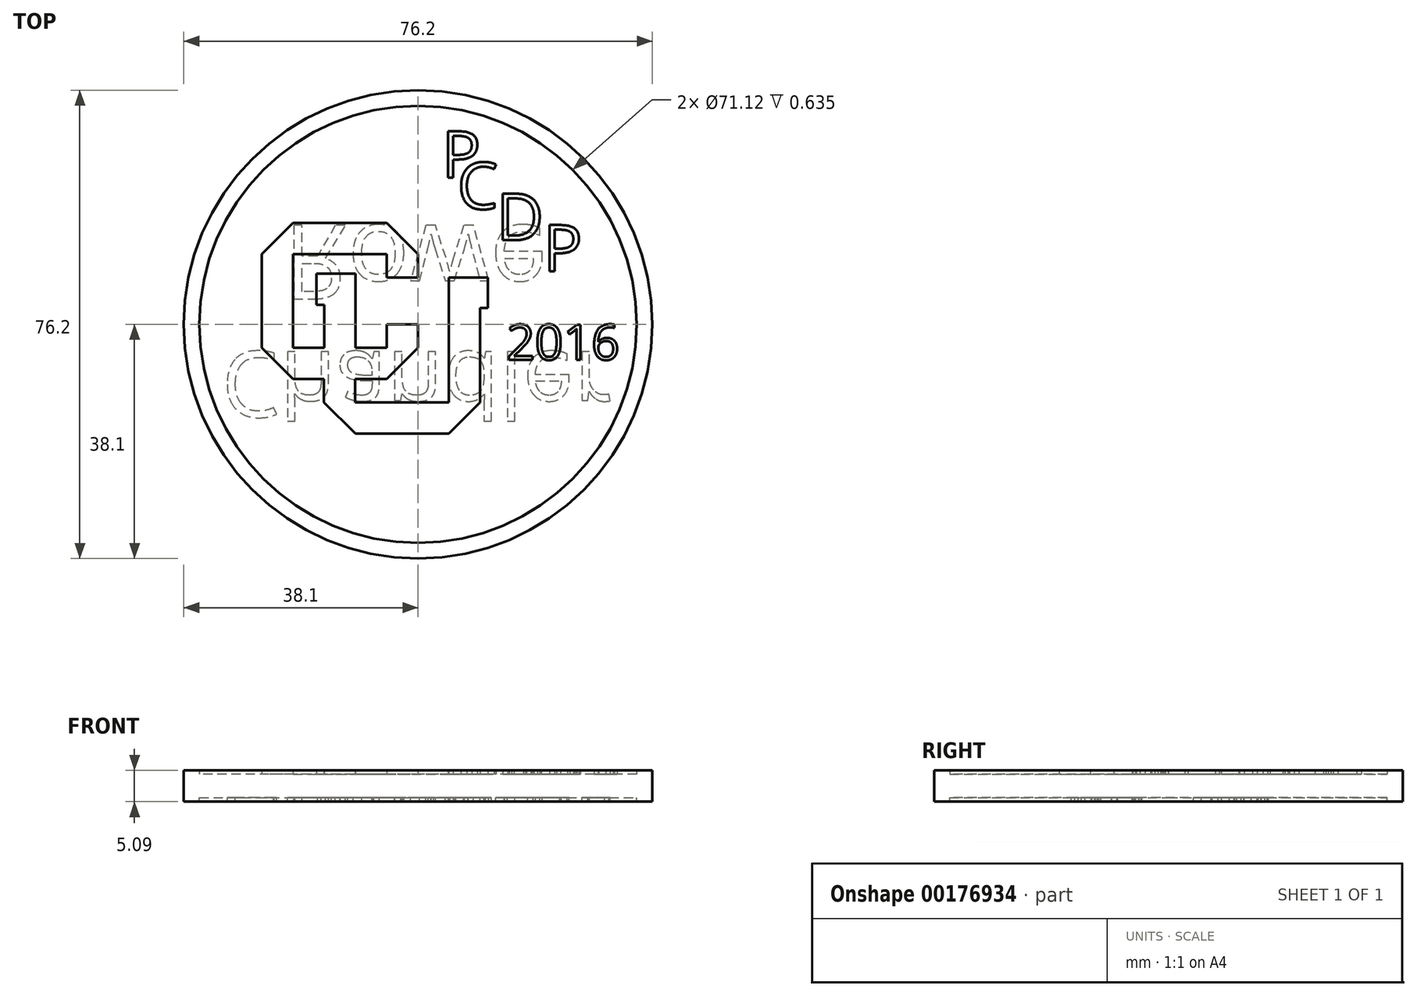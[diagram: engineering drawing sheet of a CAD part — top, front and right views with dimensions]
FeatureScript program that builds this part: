
annotation { "Feature Type Name" : "Feature", "Feature Type Description" : "" }
export const myFeature = defineFeature(function(context is Context, id is Id, definition is map)
    precondition{}
    {
        {
            var Q0;
            Q0=qCreatedBy(makeId("Top.planeOp"),FACE);
            var sketch = newSketch(context, id + "F0", { "sketchPlane" : qUnion([Q0])});
            skCircle(sketch, "E0", {"center": v(0, 0) * mm, "radius": 38.1 * mm});
            skSolve(sketch);
        }
        {
            var Q0;
            Q0=makeQuery(id+"F0.imprint","IMPRINT",FACE,{"disambiguationData":[TD([[makeQuery(id+"F0.imprint","IMPRINT",EDGE,{"derivedFrom":sQuery(id+"F0.wireOp",EDGE,"E0")}),1.0]])]});
            extrude(context, id + "F1", {"entities" : qUnion([Q0]), "depth" : 3.8 * mm});
        }
        {
            var Q0;
            Q0=makeQuery(id+"F1.opExtrude","CAP_FACE",FACE,{"disambiguationData":[OSD([sQuery(id+"F0.wireOp",EDGE,"E0")])],"isStart":false});
            var sketch = newSketch(context, id + "F2", { "sketchPlane" : qUnion([Q0])});
            skLineSegment(sketch, "E1", {"start": v(0, 0) * mm, "end": v(0, -3.81) * mm});
            skLineSegment(sketch, "E2", {"start": v(-5.08, -8.9) * mm, "end": v(0, -3.81) * mm});
            skLineSegment(sketch, "E3", {"start": v(-5.08, -8.9) * mm, "end": v(-20.32, -8.9) * mm});
            skLineSegment(sketch, "E4", {"start": v(-20.32, -8.9) * mm, "end": v(-25.4, -3.81) * mm});
            skLineSegment(sketch, "E5", {"start": v(-25.4, 11.43) * mm, "end": v(-20.32, 16.5) * mm});
            skLineSegment(sketch, "E6", {"start": v(-20.32, 16.5) * mm, "end": v(-5.08, 16.5) * mm});
            skLineSegment(sketch, "E7", {"start": v(-5.08, 16.5) * mm, "end": v(0, 11.43) * mm});
            skLineSegment(sketch, "E8", {"start": v(0, 11.43) * mm, "end": v(0, 7.62) * mm});
            skLineSegment(sketch, "E9", {"start": v(-25.4, 11.43) * mm, "end": v(-25.4, -3.81) * mm});
            skLineSegment(sketch, "E10", {"start": v(0, 7.62) * mm, "end": v(-5.08, 7.62) * mm});
            skLineSegment(sketch, "E11", {"start": v(-5.08, 7.62) * mm, "end": v(-5.08, 11.43) * mm});
            skLineSegment(sketch, "E12", {"start": v(-5.08, 11.43) * mm, "end": v(-20.32, 11.43) * mm});
            skLineSegment(sketch, "E13", {"start": v(-20.32, 11.43) * mm, "end": v(-20.32, -3.81) * mm});
            skLineSegment(sketch, "E14", {"start": v(-5.08, -3.81) * mm, "end": v(-5.08, 0) * mm});
            skLineSegment(sketch, "E15", {"start": v(-5.08, 0) * mm, "end": v(0, 0) * mm});
            skLineSegment(sketch, "E16", {"start": v(-5.08, -3.81) * mm, "end": v(-10.16, -3.81) * mm});
            skLineSegment(sketch, "E17", {"start": v(-10.16, -3.81) * mm, "end": v(-10.16, 8.25) * mm});
            skLineSegment(sketch, "E18", {"start": v(-10.16, 8.25) * mm, "end": v(-16.51, 8.25) * mm});
            skLineSegment(sketch, "E19", {"start": v(-16.51, 8.25) * mm, "end": v(-16.51, 3.17) * mm});
            skLineSegment(sketch, "E20", {"start": v(-16.51, 3.17) * mm, "end": v(-15.24, 3.17) * mm});
            skLineSegment(sketch, "E21", {"start": v(-15.24, 3.17) * mm, "end": v(-15.24, -3.81) * mm});
            skLineSegment(sketch, "E22.trimOffspring", {"start": v(-15.24, -3.81) * mm, "end": v(-20.32, -3.81) * mm});
            skLineSegment(sketch, "E23", {"start": v(-15.3, -8.9) * mm, "end": v(-15.3, -12.69) * mm});
            skLineSegment(sketch, "E24", {"start": v(-15.3, -12.69) * mm, "end": v(-10.19, -17.77) * mm});
            skLineSegment(sketch, "E25", {"start": v(-10.19, -17.77) * mm, "end": v(5.03, -17.77) * mm});
            skLineSegment(sketch, "E26", {"start": v(5.03, -17.77) * mm, "end": v(10.1, -12.69) * mm});
            skLineSegment(sketch, "E27", {"start": v(10.1, -12.69) * mm, "end": v(10.1, 2.68) * mm});
            skLineSegment(sketch, "E28", {"start": v(10.1, 2.68) * mm, "end": v(11.38, 2.68) * mm});
            skLineSegment(sketch, "E29", {"start": v(11.38, 2.68) * mm, "end": v(11.38, 7.63) * mm});
            skLineSegment(sketch, "E30", {"start": v(11.38, 7.63) * mm, "end": v(5.03, 7.63) * mm});
            skLineSegment(sketch, "E31", {"start": v(5.03, 7.63) * mm, "end": v(5.03, -12.69) * mm});
            skLineSegment(sketch, "E32", {"start": v(5.03, -12.69) * mm, "end": v(-10.21, -12.69) * mm});
            skLineSegment(sketch, "E33", {"start": v(-10.21, -12.69) * mm, "end": v(-10.21, -8.9) * mm});
            skCircle(sketch, "E34", {"center": v(0, 0) * mm, "radius": 35.56 * mm});
            skText(sketch, "E35", { "text": "P", "fontName": "OpenSans-Regular.ttf"});
            skText(sketch, "E36", { "text": "D", "fontName": "OpenSans-Regular.ttf"});
            skText(sketch, "E37", { "text": "C", "fontName": "OpenSans-Regular.ttf"});
            skText(sketch, "E38", { "text": "P", "fontName": "OpenSans-Regular.ttf"});
            skText(sketch, "E39", { "text": "2016", "fontName": "OpenSans-Regular.ttf"});
            const initialGuessF2  = {"E35": [0.0038, 0.02385, 1, 0, 0.00762], "E36": [0.0127, 0.01369, 1, 0, 0.00762], "E37": [0.00635, 0.01877, 1, 0, 0.00762], "E38": [0.02032, 0.0086, 1, 0, 0.00762], "E39": [0.0144, -0.00578, 1, 0, 0.00578]};
            skSetInitialGuess(sketch, initialGuessF2);
            skSolve(sketch);
        }
        {
            var Q0;
            Q0=makeQuery(id+"F2.imprint","IMPRINT",FACE,{"disambiguationData":[TD([[makeQuery(id+"F2.imprint","IMPRINT",EDGE,{"derivedFrom":sQuery(id+"F2.wireOp",EDGE,"E1")}),-1.0]])]});
            var Q1;
            {var subQ1=sQuery(id+"F2.wireOp",EDGE,"E23");Q1=makeQuery(id+"F2.imprint","IMPRINT",FACE,{"disambiguationData":[TD([[makeQuery(id+"F2.imprint","IMPRINT",EDGE,{"derivedFrom":subQ1}),1.0]])]});}
            var Q2;
            Q2=makeQuery(id+"F2.imprint","IMPRINT",FACE,{"disambiguationData":[TD([[makeQuery(id+"F2.imprint","IMPRINT",EDGE,{"derivedFrom":sQuery(id+"F2.wireOp",EDGE,"E34")}),-1.0]])]});
            var Q3;
            Q3=makeQuery(id+"F2.imprint","IMPRINT",FACE,{"disambiguationData":[TD([[makeQuery(id+"F2.imprint","IMPRINT",EDGE,{"derivedFrom":sQuery(id+"F2.wireOp",EDGE,"E35.sketch_text.stroke-0")}),-1.0]])]});
            var Q4;
            Q4=makeQuery(id+"F2.imprint","IMPRINT",FACE,{"disambiguationData":[TD([[makeQuery(id+"F2.imprint","IMPRINT",EDGE,{"derivedFrom":sQuery(id+"F2.wireOp",EDGE,"E37.sketch_text.stroke-0")}),-1.0]])]});
            var Q5;
            Q5=makeQuery(id+"F2.imprint","IMPRINT",FACE,{"disambiguationData":[TD([[makeQuery(id+"F2.imprint","IMPRINT",EDGE,{"derivedFrom":sQuery(id+"F2.wireOp",EDGE,"E36.sketch_text.stroke-0")}),-1.0]])]});
            var Q6;
            Q6=makeQuery(id+"F2.imprint","IMPRINT",FACE,{"disambiguationData":[TD([[makeQuery(id+"F2.imprint","IMPRINT",EDGE,{"derivedFrom":sQuery(id+"F2.wireOp",EDGE,"E38.sketch_text.stroke-0")}),-1.0]])]});
            var Q7;
            Q7=makeQuery(id+"F2.imprint","IMPRINT",FACE,{"disambiguationData":[TD([[makeQuery(id+"F2.imprint","IMPRINT",EDGE,{"derivedFrom":sQuery(id+"F2.wireOp",EDGE,"E39.sketch_text.stroke-0")}),-1.0]])]});
            var Q8;
            Q8=makeQuery(id+"F2.imprint","IMPRINT",FACE,{"disambiguationData":[TD([[makeQuery(id+"F2.imprint","IMPRINT",EDGE,{"derivedFrom":sQuery(id+"F2.wireOp",EDGE,"E39.sketch_text.stroke-20")}),-1.0]])]});
            var Q9;
            Q9=makeQuery(id+"F2.imprint","IMPRINT",FACE,{"disambiguationData":[TD([[makeQuery(id+"F2.imprint","IMPRINT",EDGE,{"derivedFrom":sQuery(id+"F2.wireOp",EDGE,"E39.sketch_text.stroke-36")}),-1.0]])]});
            var Q10;
            Q10=makeQuery(id+"F2.imprint","IMPRINT",FACE,{"disambiguationData":[TD([[makeQuery(id+"F2.imprint","IMPRINT",EDGE,{"derivedFrom":sQuery(id+"F2.wireOp",EDGE,"E39.sketch_text.stroke-45")}),-1.0]])]});
            extrude(context, id + "F3", {"entities" : qUnion([Q0, Q1, Q2, Q3, Q4, Q5, Q6, Q7, Q8, Q9, Q10]), "operationType" : NewBodyOperationType.ADD, "depth" : 0.64 * mm});
        }
        {
            var Q0;
            Q0=makeQuery(id+"F1.opExtrude","CAP_FACE",FACE,{"disambiguationData":[OSD([sQuery(id+"F0.wireOp",EDGE,"E0")])],"isStart":true});
            var sketch = newSketch(context, id + "F4", { "sketchPlane" : qUnion([Q0])});
            skCircle(sketch, "E40", {"center": v(0, 0) * mm, "radius": 35.56 * mm});
            skText(sketch, "E41", { "text": "Chandler", "fontName": "OpenSans-Regular.ttf"});
            skText(sketch, "E42", { "text": "Rowe", "fontName": "OpenSans-Regular.ttf"});
            const initialGuessF4  = {"E41": [-0.03195, 0.00443, 1, 0, 0.01074], "E42": [-0.02189, -0.0161, 1, 0, 0.01208]};
            skSetInitialGuess(sketch, initialGuessF4);
            skSolve(sketch);
        }
        {
            var Q0;
            Q0=makeQuery(id+"F4.imprint","IMPRINT",FACE,{"disambiguationData":[TD([[makeQuery(id+"F4.imprint","IMPRINT",EDGE,{"derivedFrom":sQuery(id+"F4.wireOp",EDGE,"E40")}),-1.0]])]});
            var Q1;
            Q1=makeQuery(id+"F4.imprint","IMPRINT",FACE,{"disambiguationData":[TD([[makeQuery(id+"F4.imprint","IMPRINT",EDGE,{"derivedFrom":sQuery(id+"F4.wireOp",EDGE,"E41.sketch_text.stroke-0")}),-1.0]])]});
            var Q2;
            Q2=makeQuery(id+"F4.imprint","IMPRINT",FACE,{"disambiguationData":[TD([[makeQuery(id+"F4.imprint","IMPRINT",EDGE,{"derivedFrom":sQuery(id+"F4.wireOp",EDGE,"E41.sketch_text.stroke-15")}),-1.0]])]});
            var Q3;
            Q3=makeQuery(id+"F4.imprint","IMPRINT",FACE,{"disambiguationData":[TD([[makeQuery(id+"F4.imprint","IMPRINT",EDGE,{"derivedFrom":sQuery(id+"F4.wireOp",EDGE,"E41.sketch_text.stroke-33")}),-1.0]])]});
            var Q4;
            Q4=makeQuery(id+"F4.imprint","IMPRINT",FACE,{"disambiguationData":[TD([[makeQuery(id+"F4.imprint","IMPRINT",EDGE,{"derivedFrom":sQuery(id+"F4.wireOp",EDGE,"E41.sketch_text.stroke-60")}),-1.0]])]});
            var Q5;
            Q5=makeQuery(id+"F4.imprint","IMPRINT",FACE,{"disambiguationData":[TD([[makeQuery(id+"F4.imprint","IMPRINT",EDGE,{"derivedFrom":sQuery(id+"F4.wireOp",EDGE,"E41.sketch_text.stroke-77")}),-1.0]])]});
            var Q6;
            Q6=makeQuery(id+"F4.imprint","IMPRINT",FACE,{"disambiguationData":[TD([[makeQuery(id+"F4.imprint","IMPRINT",EDGE,{"derivedFrom":sQuery(id+"F4.wireOp",EDGE,"E41.sketch_text.stroke-101")}),-1.0]])]});
            var Q7;
            Q7=makeQuery(id+"F4.imprint","IMPRINT",FACE,{"disambiguationData":[TD([[makeQuery(id+"F4.imprint","IMPRINT",EDGE,{"derivedFrom":sQuery(id+"F4.wireOp",EDGE,"E41.sketch_text.stroke-105")}),-1.0]])]});
            var Q8;
            Q8=makeQuery(id+"F4.imprint","IMPRINT",FACE,{"disambiguationData":[TD([[makeQuery(id+"F4.imprint","IMPRINT",EDGE,{"derivedFrom":sQuery(id+"F4.wireOp",EDGE,"E41.sketch_text.stroke-124")}),-1.0]])]});
            var Q9;
            Q9=makeQuery(id+"F4.imprint","IMPRINT",FACE,{"disambiguationData":[TD([[makeQuery(id+"F4.imprint","IMPRINT",EDGE,{"derivedFrom":sQuery(id+"F4.wireOp",EDGE,"E42.sketch_text.stroke-0")}),-1.0]])]});
            var Q10;
            Q10=makeQuery(id+"F4.imprint","IMPRINT",FACE,{"disambiguationData":[TD([[makeQuery(id+"F4.imprint","IMPRINT",EDGE,{"derivedFrom":sQuery(id+"F4.wireOp",EDGE,"E42.sketch_text.stroke-18")}),-1.0]])]});
            var Q11;
            Q11=makeQuery(id+"F4.imprint","IMPRINT",FACE,{"disambiguationData":[TD([[makeQuery(id+"F4.imprint","IMPRINT",EDGE,{"derivedFrom":sQuery(id+"F4.wireOp",EDGE,"E42.sketch_text.stroke-35")}),-1.0]])]});
            var Q12;
            Q12=makeQuery(id+"F4.imprint","IMPRINT",FACE,{"disambiguationData":[TD([[makeQuery(id+"F4.imprint","IMPRINT",EDGE,{"derivedFrom":sQuery(id+"F4.wireOp",EDGE,"E42.sketch_text.stroke-58")}),-1.0]])]});
            extrude(context, id + "F5", {"entities" : qUnion([Q0, Q1, Q2, Q3, Q4, Q5, Q6, Q7, Q8, Q9, Q10, Q11, Q12]), "operationType" : NewBodyOperationType.ADD, "depth" : 0.64 * mm});
        }
    });
